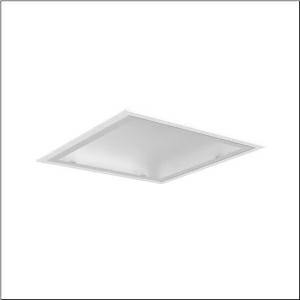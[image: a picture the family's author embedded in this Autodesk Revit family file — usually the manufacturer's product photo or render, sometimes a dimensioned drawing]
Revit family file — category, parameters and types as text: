
# Revit family: mira_r__11_51fr127a431a_8ed1
name_source: partatom
category: Lighting Fixtures
units: mm (PartAtom-declared; Revit-internal decimal feet)

## family parameters
Cut with Voids When Loaded = No
Host = Face
Light Source = No
Part Type = Normal
Room Calculation Point = No
Round Connector Dimension = Use Diameter
Shared = No

## types (1)
- Mira® 11 (1 x LED, 3060 lm, 23 W, 4000K)
    Apparent Load = 23 VA
    CIE Flux Codes = 51 82 97 100 100
    Color Rendering = 80
    Color Temperature = 4000K
    Default Elevation = 1800 mm
    Description = Mira® 11, clean room luminaire, primary light control with reflector, primary optical cover: cover, of toughened safety glass, light emission: direct distribution, primary light characteristic: symmetric, installation type: recessed, LED, rated luminous flux: 3.060lm, luminous efficacy: 133lm/W, light colour: 840, colour temperature: 4000K, control gear: ON/OFF, with terminal, 3-pole, max. 2.5mm², mains connection: 230V, AC, 50/60Hz, rated input power: 23W, luminaire housing, of sheet steel, coated, pure white (RAL 9010), with concealed magnets, module: M625, length: 623mm, width: 623mm, height: 90mm, protection rating (complete): IP65, insulation class (complete): insulation class I (protective earthing), certification: CE, UKCA, permissible operating ambient temperature: -5..+40°C, standard: EN 50419, packaging unit: 1 piece
    Height = 0 mm  [stored 0 ft]
    Lamp = 1 x LED
    Lamp Light Flux = 3060 lm
    Lamp Power = 23 W
    Lamp count = 1
    Length = 625 mm
    Luminous efficacy = 133 lm/W
    Manufacturer = Siteco
    ModVariant = No
    Model = 51FR127A431A
    Mounting Place = Ceiling
    Mounting Type = Recessed
    Number of Poles = 1
    OnlyDefault = Yes
    Power Factor = 1
    Product Name = Mira® 11
    Product group = clean room luminaire | ceiling recessed
    ProductGroupID = 402
    Protection Class = Protection class I
    Protection Degree = IP 65
    RLX_Detail_Level = 1
    RLX_Emergency_Light_Flux = 0 lm
    RLX_Emergency_Type = 0
    RLX_Emergency_Type_DB = No
    RlxData = <blob elided: 19305 chars, md5=6c0fa74b>
    Socket = socket
    Standby Power = 0 W
    System Light Flux = 3060 lm
    System Power = 23 W
    Type Comments = Product without accessories
    Type Image = l_1006636.jpg
    URL = http://relux.com
    VarID = ---
    Voltage = 0 V
    Weight = 0.00 kg
    Width = 625 mm

note: [stored X ft] marks values corroborated as IEEE doubles in the binary element streams (Revit-internal decimal feet)

## geometry (parser evidence)
native form markers: Blend x4, Sweep x11
no freeform markers — native parametric forms only
